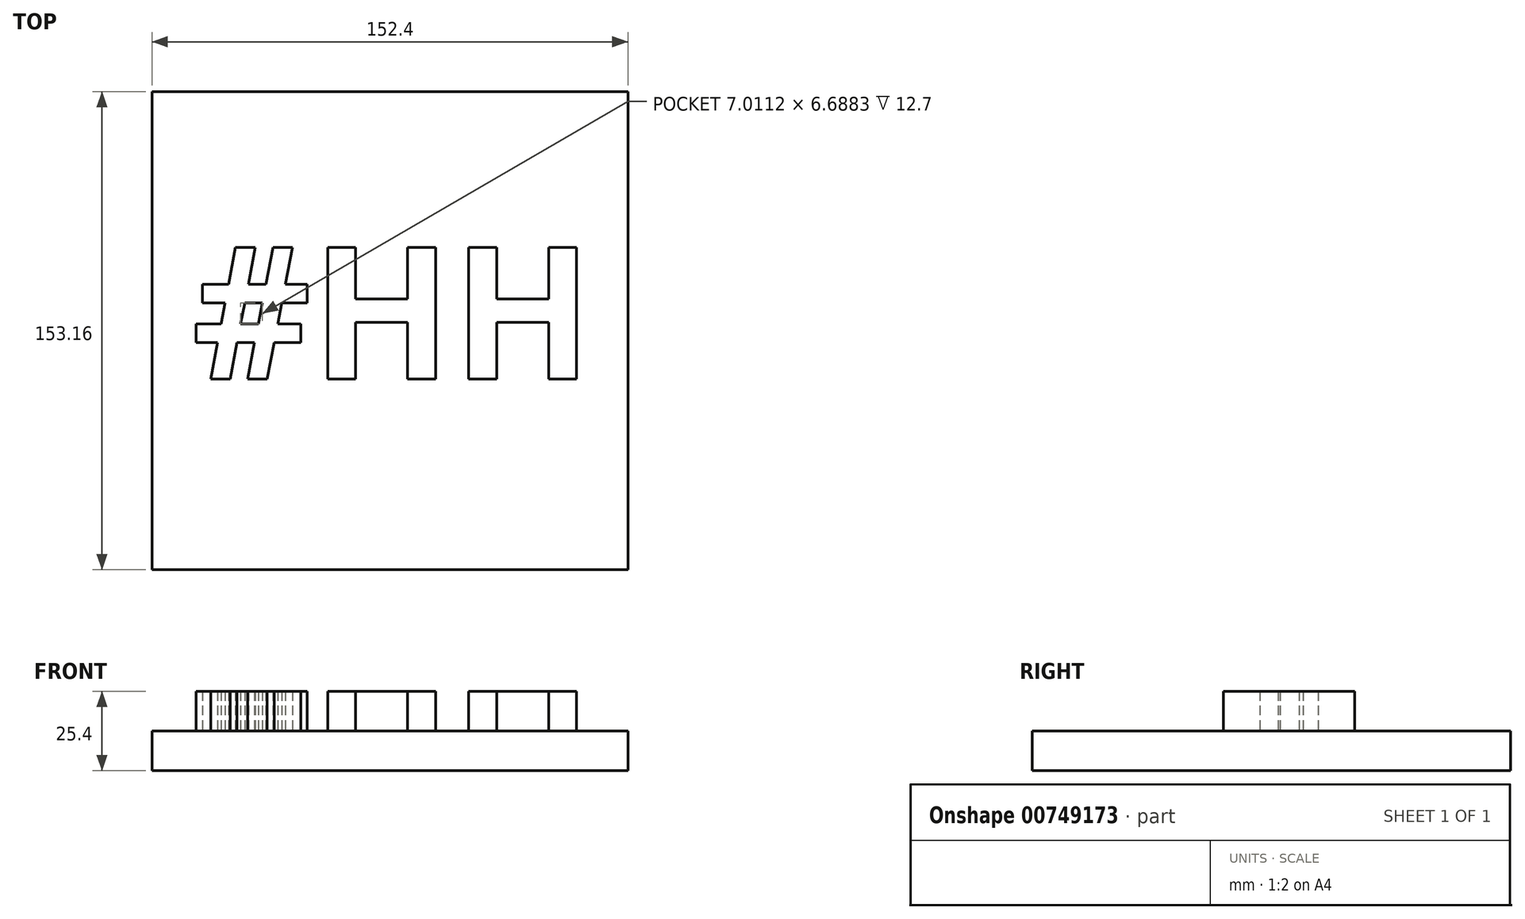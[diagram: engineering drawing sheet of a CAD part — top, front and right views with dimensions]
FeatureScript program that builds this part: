
annotation { "Feature Type Name" : "Feature", "Feature Type Description" : "" }
export const myFeature = defineFeature(function(context is Context, id is Id, definition is map)
    precondition{}
    {
        {
            var Q0;
            Q0=qCreatedBy(makeId("Top.planeOp"),FACE);
            var sketch = newSketch(context, id + "F0", { "sketchPlane" : qUnion([Q0])});
            skLineSegment(sketch, "E0.bottom", {"start": v(76.2, 76.58) * mm, "end": v(-76.2, 76.58) * mm});
            skLineSegment(sketch, "E0.top", {"start": v(76.2, -76.58) * mm, "end": v(-76.2, -76.58) * mm});
            skLineSegment(sketch, "E0.left", {"start": v(76.2, 76.58) * mm, "end": v(76.2, -76.58) * mm});
            skLineSegment(sketch, "E0.right", {"start": v(-76.2, 76.58) * mm, "end": v(-76.2, -76.58) * mm});
            skPoint(sketch, "E0.middle", {"position": v(0, 0) * mm});
            skSolve(sketch);
        }
        {
            var Q0;
            Q0 = qSketchRegion(id + "F0", true);
            extrude(context, id + "F1", {"entities" : qUnion([Q0]), "depth" : 12.7 * mm, "offsetDistance" : 25.4 * mm});
        }
        {
            var Q0;
            Q0=makeQuery(id+"F1.opExtrude","CAP_FACE",FACE,{"disambiguationData":[OSD([sQuery(id+"F0.wireOp",EDGE,"E0.bottom"),sQuery(id+"F0.wireOp",EDGE,"E0.top"),sQuery(id+"F0.wireOp",EDGE,"E0.left"),sQuery(id+"F0.wireOp",EDGE,"E0.right")])],"isStart":false});
            var sketch = newSketch(context, id + "F2", { "sketchPlane" : qUnion([Q0])});
            skText(sketch, "E1", { "text": "#HH", "fontName": "OpenSans-Bold.ttf"});
            const initialGuessF2  = {"E1": [-0.06336, -0.01548, 1, 0, 0.04251]};
            skSetInitialGuess(sketch, initialGuessF2);
            skSolve(sketch);
        }
        {
            var Q0;
            Q0 = qSketchRegion(id + "F2", true);
            extrude(context, id + "F3", {"entities" : qUnion([Q0]), "operationType" : NewBodyOperationType.ADD, "depth" : 12.7 * mm, "offsetDistance" : 25.4 * mm});
        }
    });
